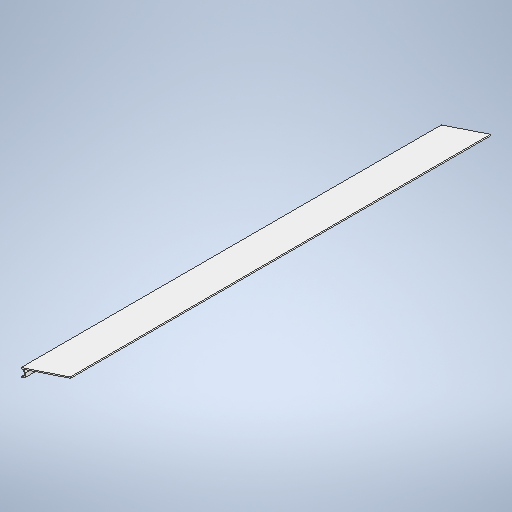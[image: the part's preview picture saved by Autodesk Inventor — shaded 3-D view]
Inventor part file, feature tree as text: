
AUTODESK INVENTOR PART (.ipt)
format: ipt  version: 2025 (Build 290162010, 162A)  size: 277,504 bytes
history: native  units: in
note: dims shown in document units (in); Inventor stores cm internally (conversion verified against a paired STEP export)
features: extrude x1, sketch x1
ambient origin geometry x8: Origin, YZ Plane, XZ Plane, XY Plane, X Axis, Y Axis, Z Axis, Center Point
bodies: Body1 (feature_tree)
feature tree (2):
  extrude  "Extrusion2"  Depth=48.752in
  sketch  "Sketch1"  dims[d5=5.5in d17=3.5in d19=132.0in d23=1.194in d28=1.8188in d33=42.875in d36=1.0in d37=0.625in d49=0.125in d50=0.125in d51=0.125in d52=0.125in d54=0.333in d55=0.333in d59=48.752in d60=0.0in d61=0.333in d62=6.0in]
